# Revit family: QF_Summit_SLS24W4P_Washer_And_Heat_Pump_Dryer_cat
name_source: partatom
category: Specialty Equipment
units: mm (PartAtom-declared; Revit-internal decimal feet)

## family parameters
Always vertical = Yes
Cut with Voids When Loaded = No
Part Type = Normal
Room Calculation Point = No
Round Connector Dimension = Use Diameter
Shared = No
Work Plane-Based = No

## types (1)
- QF_Summit_SLS24W4P_Washer_And_Heat_Pump_Dryer_cat
    Apparent Power = 0 VA
    Conn Conduit = Yes
    Conn Plug = NEMA 10-30P
    Cycle = 60 Hz
    Default Elevation = 0"
    Depth = 26 1/2"
    Description = Washer And Heat Pump Dryer
    Elec Conn Connection Height = 0"
    Elec Conn RI Height = 0"
    FL Amps = 30 A
    Foodservice Equipment Identifier = Yes
    Height = 66"
    Identify Quantity as Lot = Yes
    Indirect Waste Connection Height = 0"
    Indirect Waste Flow = 0 GPM
    Indirect Waste Size = 0"
    Length = 24"
    Manufacturer = Summit
    Max Overcurrent Protection = 0 A
    Min Ckt Ampacity = 0 A
    Model = SLS24W4P
    Number of Poles = 1
    Phase = 1
    Volts = 240 V
    Waste Water Discharge Temperature = -460 °F
    Watts = 7200 W
    Weight in Pounds = 289

## geometry (parser evidence)
native form markers: Sweep x11
no freeform markers — native parametric forms only
